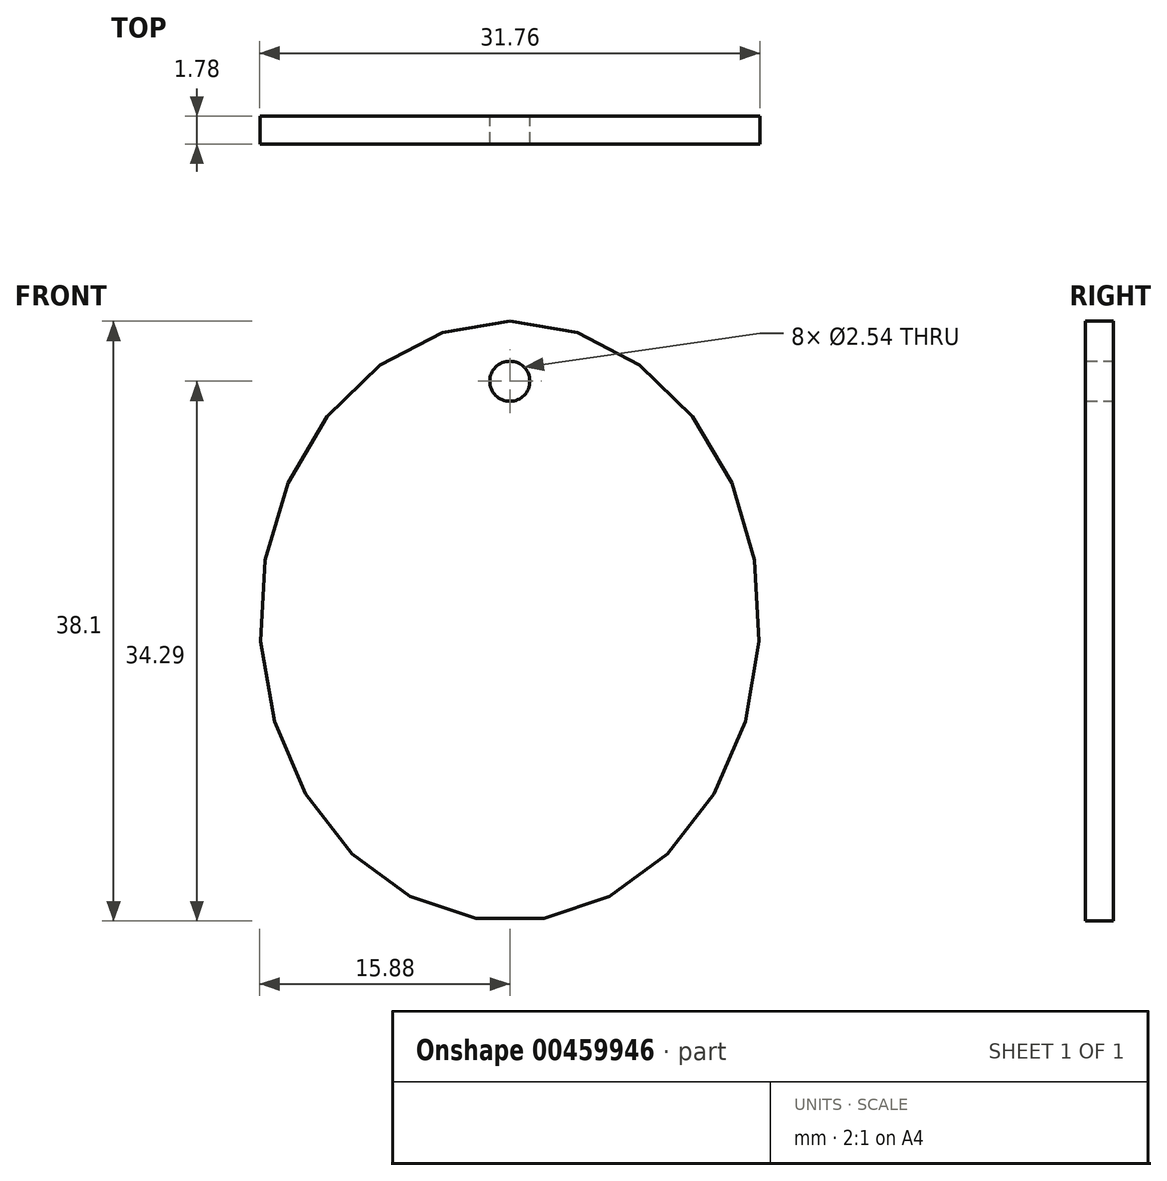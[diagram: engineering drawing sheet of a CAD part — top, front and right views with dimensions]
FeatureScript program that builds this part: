
annotation { "Feature Type Name" : "Feature", "Feature Type Description" : "" }
export const myFeature = defineFeature(function(context is Context, id is Id, definition is map)
    precondition{}
    {
        {
            var Q0;
            Q0=qCreatedBy(makeId("Front.planeOp"),FACE);
            var sketch = newSketch(context, id + "F0", { "sketchPlane" : qUnion([Q0])});
            skEllipse(sketch, "E0", {"center": v(0, 0) * mm, "majorRadius": 19.05 * mm, "minorRadius": 15.88 * mm, "majorAxis": v(0, 1)});
            skCircle(sketch, "E1", {"center": v(0, 15.24) * mm, "radius": 1.27 * mm});
            skSolve(sketch);
        }
        {
            var Q0;
            Q0 = qSketchRegion(id + "F0", true);
            extrude(context, id + "F1", {"entities" : qUnion([Q0]), "depth" : 1.78 * mm});
        }
    });
